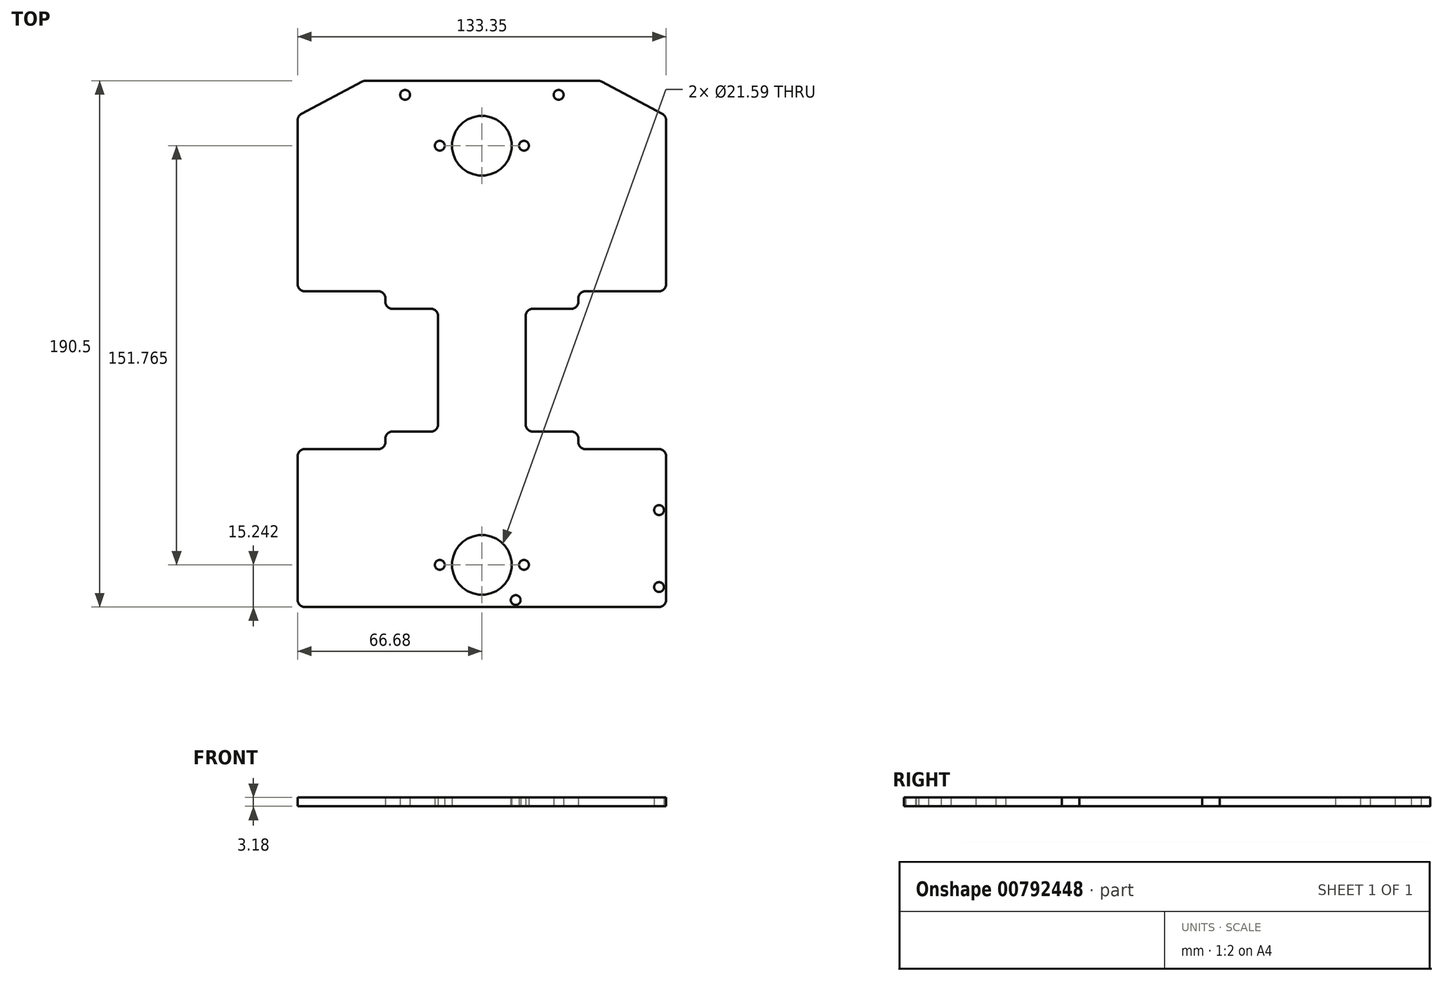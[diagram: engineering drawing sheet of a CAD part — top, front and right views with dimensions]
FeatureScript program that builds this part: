
annotation { "Feature Type Name" : "Feature", "Feature Type Description" : "" }
export const myFeature = defineFeature(function(context is Context, id is Id, definition is map)
    precondition{}
    {
        {
            var Q0;
            Q0=qCreatedBy(makeId("Top.planeOp"),FACE);
            var sketch = newSketch(context, id + "F0", { "sketchPlane" : qUnion([Q0])});
            skLineSegment(sketch, "E0.bottom", {"start": v(-136.47, -77.06) * mm, "end": v(-3.12, -77.06) * mm});
            skLineSegment(sketch, "E0.left", {"start": v(-136.47, -77.06) * mm, "end": v(-136.47, -19.9) * mm});
            skLineSegment(sketch, "E0.right", {"start": v(-3.12, -77.06) * mm, "end": v(-3.12, -19.9) * mm});
            skLineSegment(sketch, "E1", {"start": v(-136.47, 37.24) * mm, "end": v(-104.72, 37.24) * mm});
            skLineSegment(sketch, "E2", {"start": v(-104.72, 37.24) * mm, "end": v(-104.72, 30.9) * mm});
            skLineSegment(sketch, "E3", {"start": v(-104.72, -19.9) * mm, "end": v(-136.47, -19.9) * mm});
            skLineSegment(sketch, "E4", {"start": v(-3.12, 37.24) * mm, "end": v(-34.87, 37.24) * mm});
            skLineSegment(sketch, "E5", {"start": v(-34.87, 37.24) * mm, "end": v(-34.87, 30.9) * mm});
            skLineSegment(sketch, "E6", {"start": v(-34.87, -19.9) * mm, "end": v(-3.12, -19.9) * mm});
            skLineSegment(sketch, "E7.trimOffspring", {"start": v(-136.47, 37.24) * mm, "end": v(-136.47, 100.74) * mm});
            skLineSegment(sketch, "E8.trimOffspring", {"start": v(-3.12, 37.24) * mm, "end": v(-3.12, 100.74) * mm});
            skLineSegment(sketch, "E9", {"start": v(-136.47, 37.24) * mm, "end": v(-136.47, -19.9) * mm, "construction": true});
            skLineSegment(sketch, "E10", {"start": v(-3.12, 37.24) * mm, "end": v(-3.12, -19.9) * mm, "construction": true});
            skLineSegment(sketch, "E11", {"start": v(-136.47, 100.74) * mm, "end": v(-112.58, 113.44) * mm});
            skLineSegment(sketch, "E12", {"start": v(-112.58, 113.44) * mm, "end": v(-27, 113.44) * mm});
            skLineSegment(sketch, "E13", {"start": v(-27, 113.44) * mm, "end": v(-3.12, 100.74) * mm});
            skCircle(sketch, "E14", {"center": v(-85.03, -61.82) * mm, "radius": 1.79 * mm});
            skCircle(sketch, "E15", {"center": v(-54.55, -61.82) * mm, "radius": 1.79 * mm});
            skLineSegment(sketch, "E16", {"start": v(-85.03, -61.82) * mm, "end": v(-54.55, -61.82) * mm, "construction": true});
            skPoint(sketch, "E17", {"position": v(-69.8, -61.82) * mm});
            skCircle(sketch, "E18", {"center": v(-69.8, -61.82) * mm, "radius": 10.8 * mm});
            skPoint(sketch, "E19", {"position": v(-69.8, -77.06) * mm});
            skPoint(sketch, "E20", {"position": v(-69.8, 113.44) * mm});
            skCircle(sketch, "E21", {"center": v(-85.03, 89.95) * mm, "radius": 1.79 * mm});
            skCircle(sketch, "E22", {"center": v(-54.55, 89.95) * mm, "radius": 1.79 * mm});
            skLineSegment(sketch, "E23", {"start": v(-85.03, 89.95) * mm, "end": v(-54.55, 89.95) * mm, "construction": true});
            skPoint(sketch, "E24", {"position": v(-69.8, 89.95) * mm});
            skCircle(sketch, "E25", {"center": v(-69.8, 89.95) * mm, "radius": 10.8 * mm});
            skCircle(sketch, "E26", {"center": v(-97.57, 108.36) * mm, "radius": 1.79 * mm});
            skCircle(sketch, "E27", {"center": v(-42, 108.36) * mm, "radius": 1.79 * mm});
            skLineSegment(sketch, "E28", {"start": v(-97.57, 108.36) * mm, "end": v(-42, 108.36) * mm, "construction": true});
            skPoint(sketch, "E29", {"position": v(-69.8, 108.36) * mm});
            skPoint(sketch, "E30", {"position": v(-104.72, 8.67) * mm});
            skPoint(sketch, "E31", {"position": v(-34.87, 8.67) * mm});
            skPoint(sketch, "E32", {"position": v(-101.54, 8.67) * mm});
            skPoint(sketch, "E33", {"position": v(-38.04, 8.67) * mm});
            skLineSegment(sketch, "E34", {"start": v(-104.72, 30.9) * mm, "end": v(-85.67, 30.9) * mm});
            skLineSegment(sketch, "E35", {"start": v(-85.67, 30.9) * mm, "end": v(-85.67, -13.56) * mm});
            skLineSegment(sketch, "E36", {"start": v(-85.67, -13.56) * mm, "end": v(-104.72, -13.56) * mm});
            skLineSegment(sketch, "E37", {"start": v(-34.87, 30.9) * mm, "end": v(-53.92, 30.9) * mm});
            skLineSegment(sketch, "E38", {"start": v(-53.92, 30.9) * mm, "end": v(-53.92, -13.56) * mm});
            skLineSegment(sketch, "E39", {"start": v(-53.92, -13.56) * mm, "end": v(-34.87, -13.56) * mm});
            skLineSegment(sketch, "E40.trimOffspring", {"start": v(-34.87, -13.56) * mm, "end": v(-34.87, -19.9) * mm});
            skLineSegment(sketch, "E41.trimOffspring", {"start": v(-104.72, -13.56) * mm, "end": v(-104.72, -19.9) * mm});
            skPoint(sketch, "E42", {"position": v(-85.67, 8.67) * mm});
            skPoint(sketch, "E43", {"position": v(-53.92, 8.67) * mm});
            skCircle(sketch, "E44", {"center": v(-5.66, -69.87) * mm, "radius": 1.79 * mm});
            skCircle(sketch, "E45", {"center": v(-57.55, -74.57) * mm, "radius": 1.79 * mm});
            skCircle(sketch, "E46", {"center": v(-5.66, -41.98) * mm, "radius": 1.79 * mm});
            skSolve(sketch);
        }
        {
            var Q0;
            Q0=makeQuery(id+"F0.imprint","IMPRINT",FACE,{"disambiguationData":[TD([[makeQuery(id+"F0.imprint","IMPRINT",EDGE,{"derivedFrom":sQuery(id+"F0.wireOp",EDGE,"E0.bottom")}),1.0]])]});
            extrude(context, id + "F1", {"entities" : qUnion([Q0]), "depth" : 3.17 * mm, "offsetDistance" : 25.4 * mm});
        }
        {
            var Q0;
            Q0=makeQuery(id+"F1.opExtrude","SWEPT_EDGE",EDGE,{"disambiguationData":[OSD([sQuery(id+"F0.wireOp",EDGE,"E4"),sQuery(id+"F0.wireOp",EDGE,"E5")])]});
            var Q1;
            Q1=makeQuery(id+"F1.opExtrude","SWEPT_EDGE",EDGE,{"disambiguationData":[OSD([sQuery(id+"F0.wireOp",EDGE,"E5"),sQuery(id+"F0.wireOp",EDGE,"E6")])]});
            var Q2;
            Q2=makeQuery(id+"F1.opExtrude","SWEPT_EDGE",EDGE,{"disambiguationData":[OSD([sQuery(id+"F0.wireOp",EDGE,"E0.right"),sQuery(id+"F0.wireOp",EDGE,"E6")])]});
            var Q3;
            Q3=makeQuery(id+"F1.opExtrude","SWEPT_EDGE",EDGE,{"disambiguationData":[OSD([sQuery(id+"F0.wireOp",EDGE,"E4"),sQuery(id+"F0.wireOp",EDGE,"E8.trimOffspring")])]});
            var Q4;
            Q4=makeQuery(id+"F1.opExtrude","SWEPT_EDGE",EDGE,{"disambiguationData":[OSD([sQuery(id+"F0.wireOp",EDGE,"E0.bottom"),sQuery(id+"F0.wireOp",EDGE,"E0.right")])]});
            var Q5;
            Q5=makeQuery(id+"F1.opExtrude","SWEPT_EDGE",EDGE,{"disambiguationData":[OSD([sQuery(id+"F0.wireOp",EDGE,"E0.bottom"),sQuery(id+"F0.wireOp",EDGE,"E0.left")])]});
            var Q6;
            Q6=makeQuery(id+"F1.opExtrude","SWEPT_EDGE",EDGE,{"disambiguationData":[OSD([sQuery(id+"F0.wireOp",EDGE,"E8.trimOffspring"),sQuery(id+"F0.wireOp",EDGE,"E13")])]});
            var Q7;
            Q7=makeQuery(id+"F1.opExtrude","SWEPT_EDGE",EDGE,{"disambiguationData":[OSD([sQuery(id+"F0.wireOp",EDGE,"E12"),sQuery(id+"F0.wireOp",EDGE,"E13")])]});
            var Q8;
            Q8=makeQuery(id+"F1.opExtrude","SWEPT_EDGE",EDGE,{"disambiguationData":[OSD([sQuery(id+"F0.wireOp",EDGE,"E11"),sQuery(id+"F0.wireOp",EDGE,"E12")])]});
            var Q9;
            Q9=makeQuery(id+"F1.opExtrude","SWEPT_EDGE",EDGE,{"disambiguationData":[OSD([sQuery(id+"F0.wireOp",EDGE,"E7.trimOffspring"),sQuery(id+"F0.wireOp",EDGE,"E11")])]});
            var Q10;
            Q10=makeQuery(id+"F1.opExtrude","SWEPT_EDGE",EDGE,{"disambiguationData":[OSD([sQuery(id+"F0.wireOp",EDGE,"E1"),sQuery(id+"F0.wireOp",EDGE,"E7.trimOffspring")])]});
            var Q11;
            Q11=makeQuery(id+"F1.opExtrude","SWEPT_EDGE",EDGE,{"disambiguationData":[OSD([sQuery(id+"F0.wireOp",EDGE,"E1"),sQuery(id+"F0.wireOp",EDGE,"E2")])]});
            var Q12;
            Q12=makeQuery(id+"F1.opExtrude","SWEPT_EDGE",EDGE,{"disambiguationData":[OSD([sQuery(id+"F0.wireOp",EDGE,"E2"),sQuery(id+"F0.wireOp",EDGE,"E3")])]});
            var Q13;
            Q13=makeQuery(id+"F1.opExtrude","SWEPT_EDGE",EDGE,{"disambiguationData":[OSD([sQuery(id+"F0.wireOp",EDGE,"E0.left"),sQuery(id+"F0.wireOp",EDGE,"E3")])]});
            var Q14;
            Q14=makeQuery(id+"F1.opExtrude","SWEPT_EDGE",EDGE,{"disambiguationData":[OSD([sQuery(id+"F0.wireOp",EDGE,"E37"),sQuery(id+"F0.wireOp",EDGE,"E38")])]});
            var Q15;
            Q15=makeQuery(id+"F1.opExtrude","SWEPT_EDGE",EDGE,{"disambiguationData":[OSD([sQuery(id+"F0.wireOp",EDGE,"E38"),sQuery(id+"F0.wireOp",EDGE,"E39")])]});
            var Q16;
            Q16=makeQuery(id+"F1.opExtrude","SWEPT_EDGE",EDGE,{"disambiguationData":[OSD([sQuery(id+"F0.wireOp",EDGE,"E35"),sQuery(id+"F0.wireOp",EDGE,"E36")])]});
            var Q17;
            Q17=makeQuery(id+"F1.opExtrude","SWEPT_EDGE",EDGE,{"disambiguationData":[OSD([sQuery(id+"F0.wireOp",EDGE,"E36"),sQuery(id+"F0.wireOp",EDGE,"E41.trimOffspring")])]});
            var Q18;
            Q18=makeQuery(id+"F1.opExtrude","SWEPT_EDGE",EDGE,{"disambiguationData":[OSD([sQuery(id+"F0.wireOp",EDGE,"E34"),sQuery(id+"F0.wireOp",EDGE,"E35")])]});
            var Q19;
            Q19=makeQuery(id+"F1.opExtrude","SWEPT_EDGE",EDGE,{"disambiguationData":[OSD([sQuery(id+"F0.wireOp",EDGE,"E39"),sQuery(id+"F0.wireOp",EDGE,"E40.trimOffspring")])]});
            fillet(context, id + "F2", {"entities" : qUnion([Q0, Q1, Q2, Q3, Q4, Q5, Q6, Q7, Q8, Q9, Q10, Q11, Q12, Q13, Q14, Q15, Q16, Q17, Q18, Q19]), "radius" : 2.54 * mm, "tangentPropagation" : true, "allowEdgeOverflow" : false});
        }
    });
